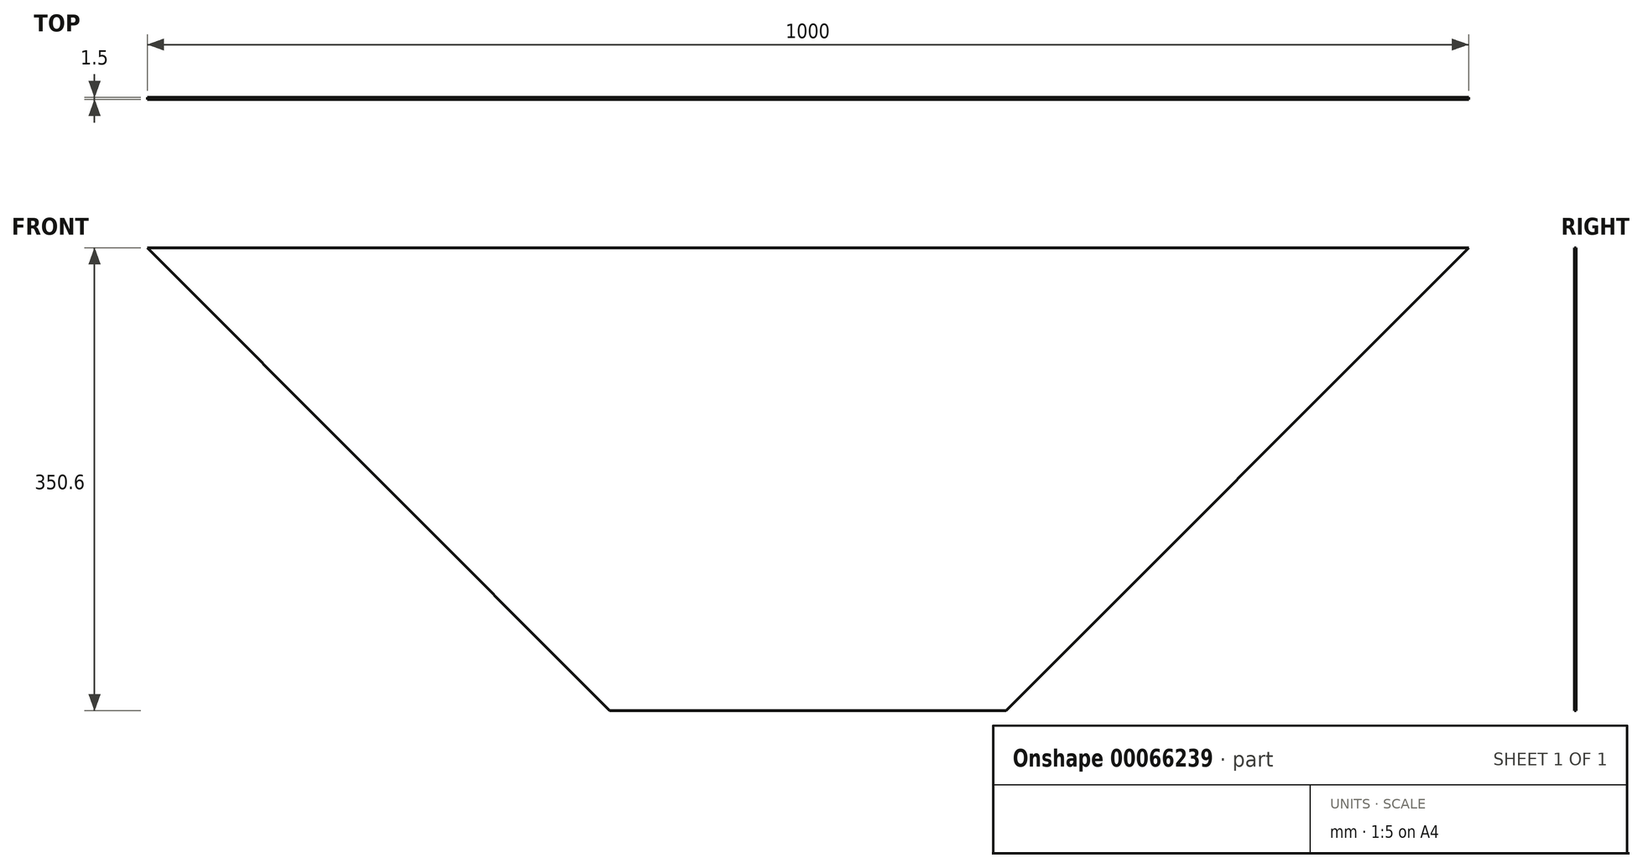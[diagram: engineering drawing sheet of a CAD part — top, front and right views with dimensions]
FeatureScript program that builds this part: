
annotation { "Feature Type Name" : "Feature", "Feature Type Description" : "" }
export const myFeature = defineFeature(function(context is Context, id is Id, definition is map)
    precondition{}
    {
        {
            var Q0;
            Q0=qCreatedBy(makeId("Front.planeOp"),FACE);
            var sketch = newSketch(context, id + "F0", { "sketchPlane" : qUnion([Q0])});
            skLineSegment(sketch, "E0", {"start": v(-516.14, 191.66) * mm, "end": v(483.86, 191.66) * mm});
            skLineSegment(sketch, "E1", {"start": v(483.86, 191.66) * mm, "end": v(133.86, -158.94) * mm});
            skLineSegment(sketch, "E2", {"start": v(133.86, -158.94) * mm, "end": v(-166.14, -158.94) * mm});
            skLineSegment(sketch, "E3", {"start": v(-166.14, -158.94) * mm, "end": v(-516.14, 191.66) * mm});
            skSolve(sketch);
        }
        {
            var Q0;
            Q0=makeQuery(id+"F0.imprint","IMPRINT",FACE,{"disambiguationData":[TD([[makeQuery(id+"F0.imprint","IMPRINT",EDGE,{"derivedFrom":sQuery(id+"F0.wireOp",EDGE,"E0")}),-1.0]])]});
            extrude(context, id + "F1", {"entities" : qUnion([Q0]), "depth" : 1.5 * mm});
        }
    });
